# Revit family: ID220
name_source: partatom
category: Apparecchi idraulici
units: mm (PartAtom-declared; Revit-internal decimal feet)

## family parameters
Basato su piano di lavoro = No
Condiviso = No
Mantieni orientamento annotazione = No
Numero OmniClass = 23.45.55.17
Punto di calcolo locali = No
Quota connettore circolare = Usa diametro
Sempre verticale = Sì
Taglio con vuoti quando caricato = No
Tipo di parte = Normale
Titolo OmniClass = Mixing Faucets

## types (12) — shared parameters
Cold water inlet = 10 mm  [stored 0.0328084 ft]
Commenti sul tipo = Bidet mixer
Connessione CW = No
Connessione HW = No
Connessione di scarico = No
Connessione di ventilazione = No
Descrizione = Monohole bidet mixer complete with drain
Hot water inlet = 10 mm  [stored 0.0328084 ft]
Produttore = IB Rubinetterie S.p.A.
URL = https://www.weareib.it
zero-valued in all types: Prospetto di default

## per-type parameters (varying)
| type | Finishes surface | Immagine tipo | Modello |
| Chrome | IB_Chrome | ID220CC.jpg | ID220CC |
| Brushed nickel | IB_Brushed nickel | ID220SS.jpg | ID220SS |
| Matt black | IB_matt black | ID220NP.jpg | ID220NP |
| Natural brass | IB_Brass | ID220ON.jpg | ID220ON |
| Black chrome | IB_Black chrome | ID220CF.jpg | ID220CF |
| Brushed black chrome | IB_Brushed black chrome | ID220CS.jpg | ID220CS |
| Pale gold | IB_Pale gold | ID220II.jpg | ID220II |
| Brushed pale gold | IB_brushed pale gold | ID220IS.jpg | ID220IS |
| Rose gold | IB_Rose gold | ID220RS.jpg | ID220RS |
| Brushed rose gold | IB_Brushed rose gold | ID220SR.jpg | ID220SR |
| Gold | IB_gold | ID220OO.jpg | ID220OO |
| Brushed gold | IB_brushed gold | ID220OS.jpg | ID220OS |

note: [stored X ft] marks values corroborated as IEEE doubles in the binary element streams (Revit-internal decimal feet)
